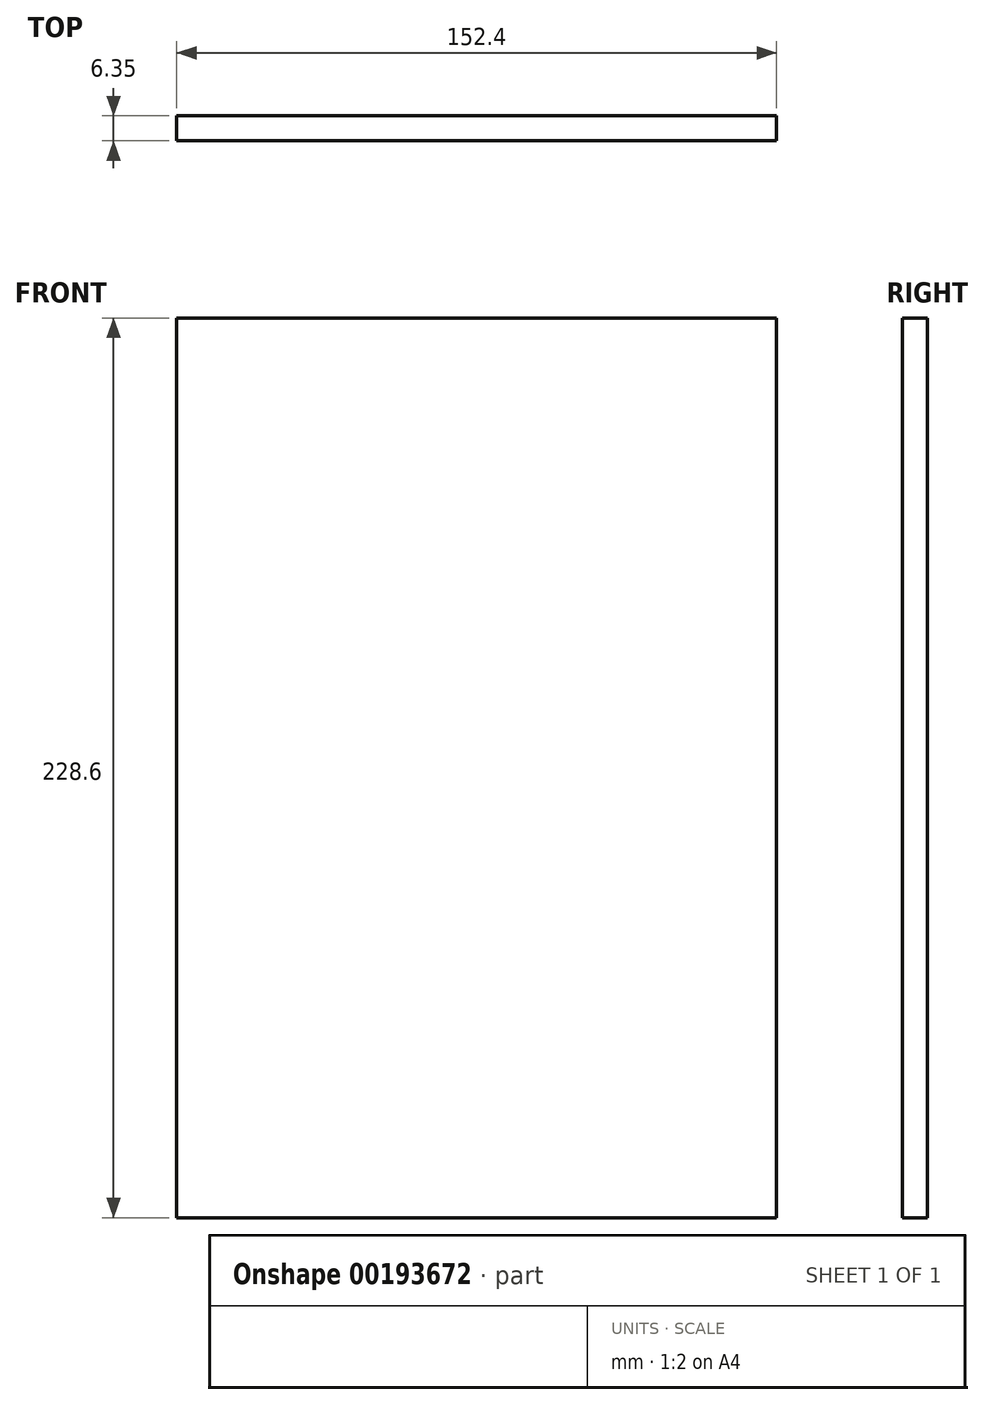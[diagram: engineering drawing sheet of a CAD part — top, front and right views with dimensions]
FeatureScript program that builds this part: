
annotation { "Feature Type Name" : "Feature", "Feature Type Description" : "" }
export const myFeature = defineFeature(function(context is Context, id is Id, definition is map)
    precondition{}
    {
        {
            var Q0;
            Q0=qCreatedBy(makeId("Front.planeOp"),FACE);
            var sketch = newSketch(context, id + "F0", { "sketchPlane" : qUnion([Q0])});
            skLineSegment(sketch, "E0.bottom", {"start": v(-76.2, -114.3) * mm, "end": v(76.2, -114.3) * mm});
            skLineSegment(sketch, "E0.top", {"start": v(-76.2, 114.3) * mm, "end": v(76.2, 114.3) * mm});
            skLineSegment(sketch, "E0.left", {"start": v(-76.2, -114.3) * mm, "end": v(-76.2, 114.3) * mm});
            skLineSegment(sketch, "E0.right", {"start": v(76.2, -114.3) * mm, "end": v(76.2, 114.3) * mm});
            skPoint(sketch, "E0.middle", {"position": v(0, 0) * mm});
            skSolve(sketch);
        }
        {
            var Q0;
            Q0 = qSketchRegion(id + "F0", true);
            extrude(context, id + "F1", {"entities" : qUnion([Q0]), "depth" : 6.35 * mm});
        }
    });
